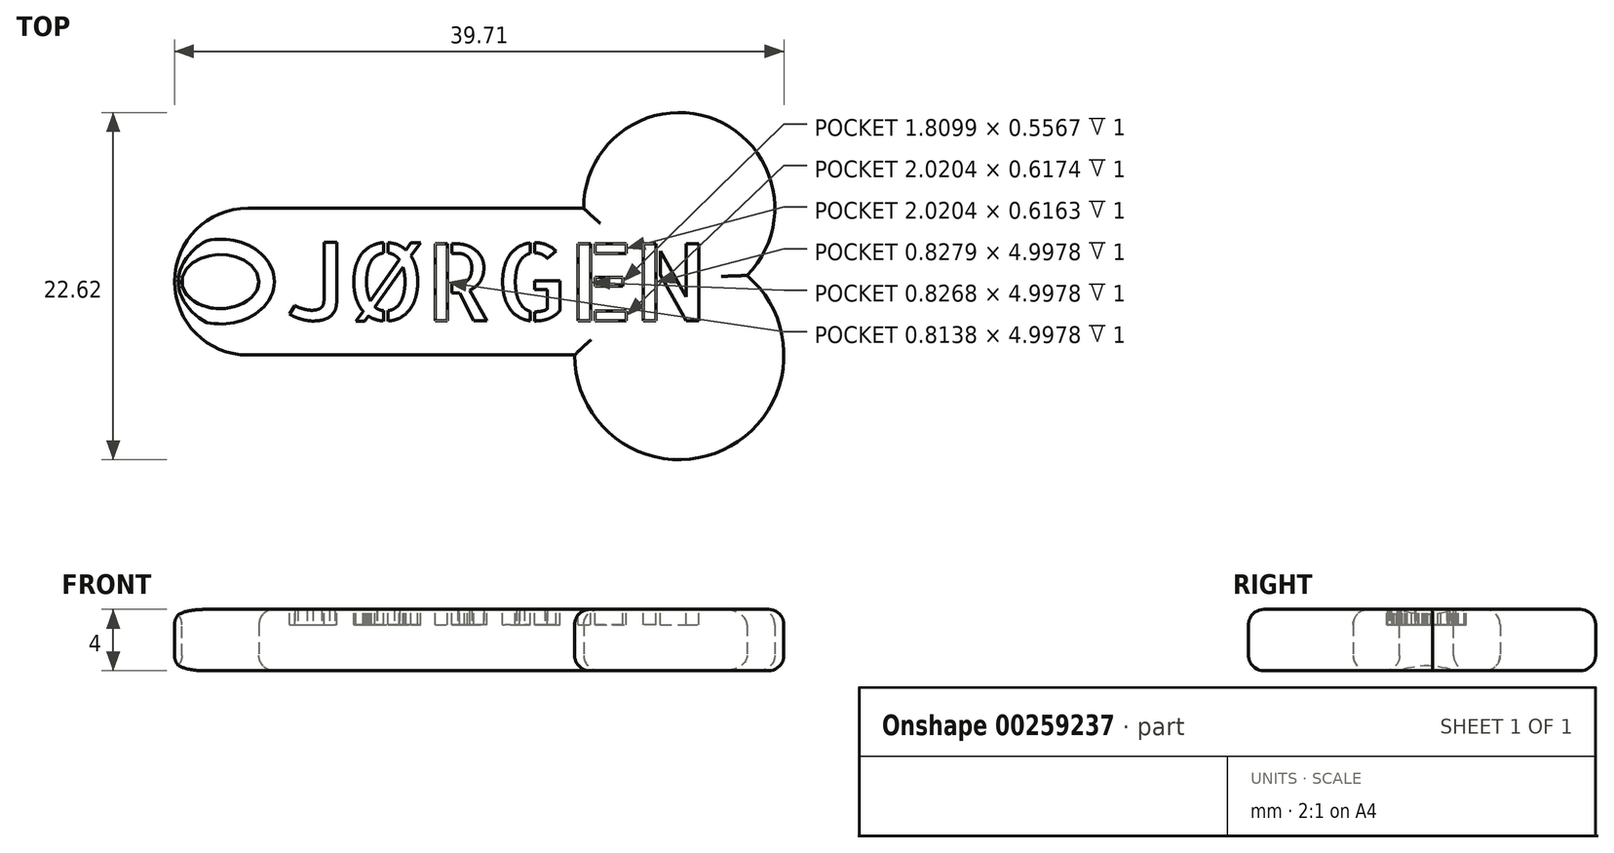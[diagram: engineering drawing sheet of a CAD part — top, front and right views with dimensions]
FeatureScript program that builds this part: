
annotation { "Feature Type Name" : "Feature", "Feature Type Description" : "" }
export const myFeature = defineFeature(function(context is Context, id is Id, definition is map)
    precondition{}
    {
        {
            var Q0;
            Q0=qCreatedBy(makeId("Top.planeOp"),FACE);
            var sketch = newSketch(context, id + "F0", { "sketchPlane" : qUnion([Q0])});
            skLineSegment(sketch, "E0.bottom", {"start": v(4.79, -14.05) * mm, "end": v(-4.79, -14.05) * mm});
            skLineSegment(sketch, "E0.top", {"start": v(4.79, 14.05) * mm, "end": v(-4.79, 14.05) * mm});
            skLineSegment(sketch, "E0.left", {"start": v(4.79, -14.05) * mm, "end": v(4.79, 14.05) * mm});
            skLineSegment(sketch, "E0.right", {"start": v(-4.79, -14.05) * mm, "end": v(-4.79, 14.05) * mm});
            skPoint(sketch, "E0.middle", {"position": v(0, 0) * mm});
            skCircle(sketch, "E1", {"center": v(4.79, -14.05) * mm, "radius": 6.23 * mm});
            skCircle(sketch, "E2", {"center": v(-4.79, -14.05) * mm, "radius": 6.82 * mm});
            skCircle(sketch, "E3", {"center": v(0, 14.05) * mm, "radius": 4.79 * mm});
            skEllipse(sketch, "E4", {"center": v(0, 15.85) * mm, "majorRadius": 2.51 * mm, "minorRadius": 1.76 * mm, "majorAxis": v(0, -1)});
            skSolve(sketch);
        }
        {
            var Q0;
            {var subQ0=sQuery(id+"F0.wireOp",EDGE,"E0.top");Q0=makeQuery(id+"F0.imprint","IMPRINT",FACE,{"disambiguationData":[TD([[makeQuery(id+"F0.imprint","IMPRINT",EDGE,{"derivedFrom":subQ0}),1.0]])]});}
            var Q1;
            {var subQ0=sQuery(id+"F0.wireOp",EDGE,"E0.top");Q1=makeQuery(id+"F0.imprint","IMPRINT",FACE,{"disambiguationData":[TD([[makeQuery(id+"F0.imprint","IMPRINT",EDGE,{"derivedFrom":subQ0}),-1.0]])]});}
            var Q2;
            {var subQ3=sQuery(id+"F0.wireOp",EDGE,"E1");var subQ6=sQuery(id+"F0.wireOp",EDGE,"E0.left");var subQ10=makeQuery(id+"F0.imprint","INTERSECT",VERTEX,{"derivedFrom":[subQ6,subQ3]});Q2=makeQuery(id+"F0.imprint","IMPRINT",FACE,{"disambiguationData":[TD([[makeQuery(id+"F0.imprint","IMPRINT",EDGE,{"disambiguationData":[TD([[subQ10,-1.0]])],"derivedFrom":subQ3}),-1.0]])]});}
            var Q3;
            {var subQ0=sQuery(id+"F0.wireOp",EDGE,"E0.left");var subQ1=sQuery(id+"F0.wireOp",EDGE,"E0.bottom");var subQ2=makeQuery(id+"F0.imprint","INTERSECT",VERTEX,{"derivedFrom":[subQ1,subQ0]});Q3=makeQuery(id+"F0.imprint","IMPRINT",FACE,{"disambiguationData":[TD([[makeQuery(id+"F0.imprint","IMPRINT",EDGE,{"disambiguationData":[TD([[subQ2,-1.0]])],"derivedFrom":subQ1}),1.0]])]});}
            var Q4;
            {var subQ0=sQuery(id+"F0.wireOp",EDGE,"E0.left");var subQ1=sQuery(id+"F0.wireOp",EDGE,"E0.bottom");var subQ2=makeQuery(id+"F0.imprint","INTERSECT",VERTEX,{"derivedFrom":[subQ1,subQ0]});Q4=makeQuery(id+"F0.imprint","IMPRINT",FACE,{"disambiguationData":[TD([[makeQuery(id+"F0.imprint","IMPRINT",EDGE,{"disambiguationData":[TD([[subQ2,-1.0]])],"derivedFrom":subQ1}),-1.0]])]});}
            var Q5;
            {var subQ0=sQuery(id+"F0.wireOp",EDGE,"E2");var subQ1=sQuery(id+"F0.wireOp",EDGE,"E0.bottom");var subQ2=makeQuery(id+"F0.imprint","INTERSECT",VERTEX,{"derivedFrom":[subQ1,subQ0]});Q5=makeQuery(id+"F0.imprint","IMPRINT",FACE,{"disambiguationData":[TD([[makeQuery(id+"F0.imprint","IMPRINT",EDGE,{"disambiguationData":[TD([[subQ2,-1.0]])],"derivedFrom":subQ1}),-1.0]])]});}
            var Q6;
            {var subQ0=sQuery(id+"F0.wireOp",EDGE,"E0.right");var subQ1=sQuery(id+"F0.wireOp",EDGE,"E0.bottom");var subQ2=makeQuery(id+"F0.imprint","INTERSECT",VERTEX,{"derivedFrom":[subQ1,subQ0]});Q6=makeQuery(id+"F0.imprint","IMPRINT",FACE,{"disambiguationData":[TD([[makeQuery(id+"F0.imprint","IMPRINT",EDGE,{"disambiguationData":[TD([[subQ2,1.0]])],"derivedFrom":subQ1}),-1.0]])]});}
            var Q7;
            {var subQ0=sQuery(id+"F0.wireOp",EDGE,"E0.right");var subQ1=sQuery(id+"F0.wireOp",EDGE,"E0.bottom");var subQ2=makeQuery(id+"F0.imprint","INTERSECT",VERTEX,{"derivedFrom":[subQ1,subQ0]});Q7=makeQuery(id+"F0.imprint","IMPRINT",FACE,{"disambiguationData":[TD([[makeQuery(id+"F0.imprint","IMPRINT",EDGE,{"disambiguationData":[TD([[subQ2,1.0]])],"derivedFrom":subQ1}),1.0]])]});}
            var Q8;
            {var subQ0=sQuery(id+"F0.wireOp",EDGE,"E2");var subQ1=sQuery(id+"F0.wireOp",EDGE,"E0.bottom");var subQ2=makeQuery(id+"F0.imprint","INTERSECT",VERTEX,{"derivedFrom":[subQ1,subQ0]});Q8=makeQuery(id+"F0.imprint","IMPRINT",FACE,{"disambiguationData":[TD([[makeQuery(id+"F0.imprint","IMPRINT",EDGE,{"disambiguationData":[TD([[subQ2,-1.0]])],"derivedFrom":subQ1}),1.0]])]});}
            extrude(context, id + "F1", {"entities" : qUnion([Q0, Q1, Q2, Q3, Q4, Q5, Q6, Q7, Q8]), "depth" : 4 * mm, "offsetDistance" : 25 * mm});
        }
        {
            var Q0;
            Q0=makeQuery(id+"F1.opExtrude","CAP_EDGE",EDGE,{"disambiguationData":[OSD([sQuery(id+"F0.wireOp",EDGE,"E0.right")])],"isStart":false});
            var Q1;
            Q1=makeQuery(id+"F1.opExtrude","CAP_EDGE",EDGE,{"disambiguationData":[OSD([sQuery(id+"F0.wireOp",EDGE,"E0.right")])],"isStart":true});
            var Q2;
            Q2=makeQuery(id+"F1.opExtrude","CAP_EDGE",EDGE,{"disambiguationData":[OSD([sQuery(id+"F0.wireOp",EDGE,"E3")])],"isStart":true});
            var Q3;
            Q3=makeQuery(id+"F1.opExtrude","CAP_EDGE",EDGE,{"disambiguationData":[OSD([sQuery(id+"F0.wireOp",EDGE,"E3")])],"isStart":false});
            var Q4;
            Q4=makeQuery(id+"F1.opExtrude","CAP_EDGE",EDGE,{"disambiguationData":[OSD([sQuery(id+"F0.wireOp",EDGE,"E0.left")])],"isStart":false});
            var Q5;
            Q5=makeQuery(id+"F1.opExtrude","CAP_EDGE",EDGE,{"disambiguationData":[OSD([sQuery(id+"F0.wireOp",EDGE,"E0.left")])],"isStart":true});
            var Q6;
            Q6=makeQuery(id+"F1.opExtrude","CAP_EDGE",EDGE,{"disambiguationData":[OSD([sQuery(id+"F0.wireOp",EDGE,"E4")])],"isStart":false});
            var Q7;
            Q7=makeQuery(id+"F1.opExtrude","CAP_EDGE",EDGE,{"disambiguationData":[OSD([sQuery(id+"F0.wireOp",EDGE,"E4")])],"isStart":true});
            var Q8;
            Q8=makeQuery(id+"F1.opExtrude","CAP_EDGE",EDGE,{"disambiguationData":[OSD([sQuery(id+"F0.wireOp",EDGE,"E2")])],"isStart":true});
            var Q9;
            Q9=makeQuery(id+"F1.opExtrude","CAP_EDGE",EDGE,{"disambiguationData":[OSD([sQuery(id+"F0.wireOp",EDGE,"E1")])],"isStart":true});
            var Q10;
            Q10=makeQuery(id+"F1.opExtrude","CAP_EDGE",EDGE,{"disambiguationData":[OSD([sQuery(id+"F0.wireOp",EDGE,"E2")])],"isStart":false});
            var Q11;
            Q11=makeQuery(id+"F1.opExtrude","CAP_EDGE",EDGE,{"disambiguationData":[OSD([sQuery(id+"F0.wireOp",EDGE,"E1")])],"isStart":false});
            fillet(context, id + "F2", {"entities" : qUnion([Q0, Q1, Q2, Q3, Q4, Q5, Q6, Q7, Q8, Q9, Q10, Q11]), "radius" : 1 * mm, "tangentPropagation" : true, "allowEdgeOverflow" : false});
        }
        {
            var Q0;
            Q0=makeQuery(id+"F1.opExtrude","SWEPT_BODY",BODY,{"disambiguationData":[OSD([sQuery(id+"F0.wireOp",EDGE,"E0.left"),sQuery(id+"F0.wireOp",EDGE,"E0.right"),sQuery(id+"F0.wireOp",EDGE,"E1"),sQuery(id+"F0.wireOp",EDGE,"E2"),sQuery(id+"F0.wireOp",EDGE,"E3"),sQuery(id+"F0.wireOp",EDGE,"E4")])]});
            var Q1;
            {var subQ0=sQuery(id+"F0.wireOp",EDGE,"E2");Q1=makeQuery(id+"F2.opFillet","BLEND_FACE",FACE,{"disambiguationData":[OSD([subQ0]),TDD([makeQuery(id+"F1.opExtrude","CAP_EDGE",EDGE,{"disambiguationData":[OSD([subQ0])],"isStart":false})])]});}
            transform(context, id + "F3", {"entities" : qUnion([Q0]), "transformType" : TransformType.ROTATION, "transformAxis" : qUnion([Q1]), "angle" : 90 * degree, "makeCopy" : false});
        }
        {
            var Q0;
            Q0=makeQuery(id+"F1.opExtrude","CAP_FACE",FACE,{"disambiguationData":[OSD([sQuery(id+"F0.wireOp",EDGE,"E0.left"),sQuery(id+"F0.wireOp",EDGE,"E0.right"),sQuery(id+"F0.wireOp",EDGE,"E1"),sQuery(id+"F0.wireOp",EDGE,"E2"),sQuery(id+"F0.wireOp",EDGE,"E3"),sQuery(id+"F0.wireOp",EDGE,"E4")])],"isStart":false});
            var sketch = newSketch(context, id + "F4", { "sketchPlane" : qUnion([Q0])});
            skText(sketch, "E5", { "text": "JORGEN", "fontName": "AllertaStencil-Regular.ttf"});
            const initialGuessF4  = {"E5": [-0.03035, -0.0118, 1, 0, 0.005]};
            skSetInitialGuess(sketch, initialGuessF4);
            skSolve(sketch);
        }
        {
            var Q0;
            Q0=makeQuery(id+"F1.opExtrude","CAP_FACE",FACE,{"disambiguationData":[OSD([sQuery(id+"F0.wireOp",EDGE,"E0.left"),sQuery(id+"F0.wireOp",EDGE,"E0.right"),sQuery(id+"F0.wireOp",EDGE,"E1"),sQuery(id+"F0.wireOp",EDGE,"E2"),sQuery(id+"F0.wireOp",EDGE,"E3"),sQuery(id+"F0.wireOp",EDGE,"E4")])],"isStart":false});
            var sketch = newSketch(context, id + "F5", { "sketchPlane" : qUnion([Q0])});
            skLineSegment(sketch, "E6", {"start": v(-22.26, -6.73) * mm, "end": v(-25.85, -11.86) * mm});
            skLineSegment(sketch, "E7", {"start": v(-25.85, -11.86) * mm, "end": v(-25.3, -11.86) * mm});
            skLineSegment(sketch, "E8", {"start": v(-25.3, -11.86) * mm, "end": v(-21.65, -6.73) * mm});
            skLineSegment(sketch, "E9", {"start": v(-21.65, -6.73) * mm, "end": v(-22.26, -6.73) * mm});
            skSolve(sketch);
        }
        {
            var Q0;
            Q0=makeQuery(id+"F4.imprint","IMPRINT",FACE,{"disambiguationData":[TD([[makeQuery(id+"F4.imprint","IMPRINT",EDGE,{"derivedFrom":sQuery(id+"F4.wireOp",EDGE,"E5.sketch_text.stroke-0")}),-1.0]])]});
            var Q1;
            Q1=makeQuery(id+"F4.imprint","IMPRINT",FACE,{"disambiguationData":[TD([[makeQuery(id+"F4.imprint","IMPRINT",EDGE,{"derivedFrom":sQuery(id+"F4.wireOp",EDGE,"E5.sketch_text.stroke-18")}),-1.0]])]});
            var Q2;
            Q2=makeQuery(id+"F4.imprint","IMPRINT",FACE,{"disambiguationData":[TD([[makeQuery(id+"F4.imprint","IMPRINT",EDGE,{"derivedFrom":sQuery(id+"F4.wireOp",EDGE,"E5.sketch_text.stroke-36")}),-1.0]])]});
            var Q3;
            Q3=makeQuery(id+"F4.imprint","IMPRINT",FACE,{"disambiguationData":[TD([[makeQuery(id+"F4.imprint","IMPRINT",EDGE,{"derivedFrom":sQuery(id+"F4.wireOp",EDGE,"E5.sketch_text.stroke-54")}),-1.0]])]});
            var Q4;
            Q4=makeQuery(id+"F4.imprint","IMPRINT",FACE,{"disambiguationData":[TD([[makeQuery(id+"F4.imprint","IMPRINT",EDGE,{"derivedFrom":sQuery(id+"F4.wireOp",EDGE,"E5.sketch_text.stroke-58")}),-1.0]])]});
            var Q5;
            Q5=makeQuery(id+"F4.imprint","IMPRINT",FACE,{"disambiguationData":[TD([[makeQuery(id+"F4.imprint","IMPRINT",EDGE,{"derivedFrom":sQuery(id+"F4.wireOp",EDGE,"E5.sketch_text.stroke-92")}),-1.0]])]});
            var Q6;
            Q6=makeQuery(id+"F4.imprint","IMPRINT",FACE,{"disambiguationData":[TD([[makeQuery(id+"F4.imprint","IMPRINT",EDGE,{"derivedFrom":sQuery(id+"F4.wireOp",EDGE,"E5.sketch_text.stroke-84")}),-1.0]])]});
            var Q7;
            Q7=makeQuery(id+"F4.imprint","IMPRINT",FACE,{"disambiguationData":[TD([[makeQuery(id+"F4.imprint","IMPRINT",EDGE,{"derivedFrom":sQuery(id+"F4.wireOp",EDGE,"E5.sketch_text.stroke-110")}),-1.0]])]});
            var Q8;
            Q8=makeQuery(id+"F4.imprint","IMPRINT",FACE,{"disambiguationData":[TD([[makeQuery(id+"F4.imprint","IMPRINT",EDGE,{"derivedFrom":sQuery(id+"F4.wireOp",EDGE,"E5.sketch_text.stroke-125")}),-1.0]])]});
            var Q9;
            Q9=makeQuery(id+"F4.imprint","IMPRINT",FACE,{"disambiguationData":[TD([[makeQuery(id+"F4.imprint","IMPRINT",EDGE,{"derivedFrom":sQuery(id+"F4.wireOp",EDGE,"E5.sketch_text.stroke-129")}),-1.0]])]});
            var Q10;
            Q10=makeQuery(id+"F4.imprint","IMPRINT",FACE,{"disambiguationData":[TD([[makeQuery(id+"F4.imprint","IMPRINT",EDGE,{"derivedFrom":sQuery(id+"F4.wireOp",EDGE,"E5.sketch_text.stroke-133")}),-1.0]])]});
            var Q11;
            Q11=makeQuery(id+"F4.imprint","IMPRINT",FACE,{"disambiguationData":[TD([[makeQuery(id+"F4.imprint","IMPRINT",EDGE,{"derivedFrom":sQuery(id+"F4.wireOp",EDGE,"E5.sketch_text.stroke-137")}),-1.0]])]});
            var Q12;
            Q12=makeQuery(id+"F4.imprint","IMPRINT",FACE,{"disambiguationData":[TD([[makeQuery(id+"F4.imprint","IMPRINT",EDGE,{"derivedFrom":sQuery(id+"F4.wireOp",EDGE,"E5.sketch_text.stroke-148")}),-1.0]])]});
            var Q13;
            Q13=makeQuery(id+"F4.imprint","IMPRINT",FACE,{"disambiguationData":[TD([[makeQuery(id+"F4.imprint","IMPRINT",EDGE,{"derivedFrom":sQuery(id+"F4.wireOp",EDGE,"E5.sketch_text.stroke-141")}),-1.0]])]});
            extrude(context, id + "F6", {"entities" : qUnion([Q0, Q1, Q2, Q3, Q4, Q5, Q6, Q7, Q8, Q9, Q10, Q11, Q12, Q13]), "operationType" : NewBodyOperationType.REMOVE, "oppositeDirection" : true, "depth" : 1 * mm});
        }
        {
            var Q0;
            Q0=makeQuery(id+"F5.imprint","IMPRINT",FACE,{"disambiguationData":[TD([[makeQuery(id+"F5.imprint","IMPRINT",EDGE,{"derivedFrom":sQuery(id+"F5.wireOp",EDGE,"E6")}),1.0]])]});
            extrude(context, id + "F7", {"entities" : qUnion([Q0]), "operationType" : NewBodyOperationType.REMOVE, "oppositeDirection" : true, "depth" : 1 * mm});
        }
    });
